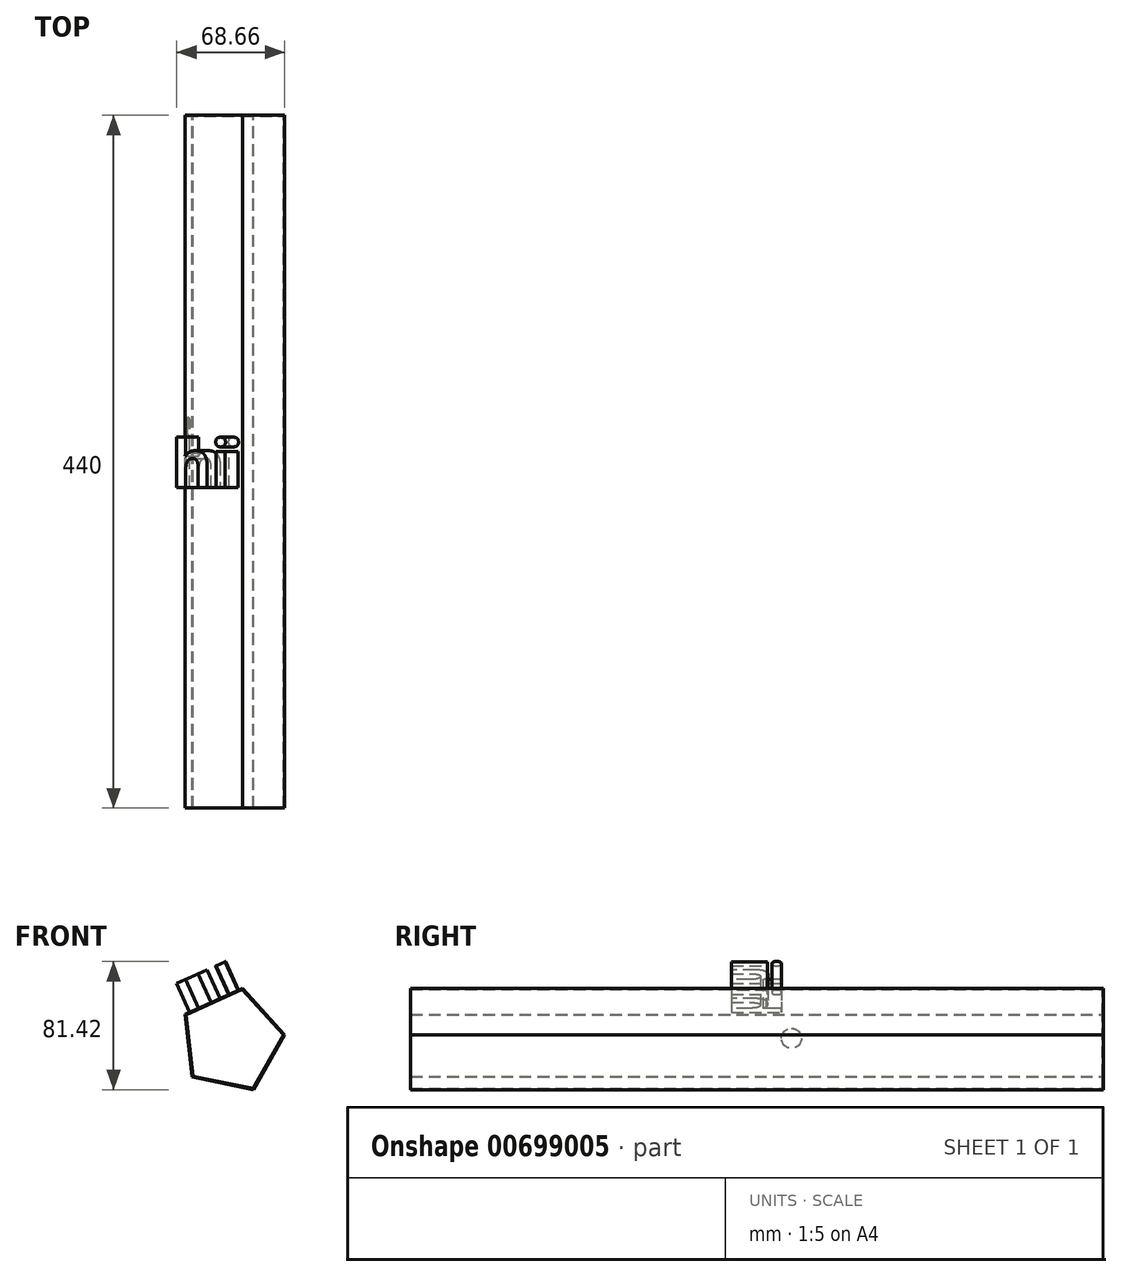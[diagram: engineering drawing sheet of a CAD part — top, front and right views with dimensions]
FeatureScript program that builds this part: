
annotation { "Feature Type Name" : "Feature", "Feature Type Description" : "" }
export const myFeature = defineFeature(function(context is Context, id is Id, definition is map)
    precondition{}
    {
        {
            var Q0;
            Q0=qCreatedBy(makeId("Front.planeOp"),FACE);
            var sketch = newSketch(context, id + "F0", { "sketchPlane" : qUnion([Q0])});
            skCircle(sketch, "E0.cCircle", {"center": v(19.03, -2.53) * mm, "radius": 27.53 * mm, "construction": true});
            skLineSegment(sketch, "E0.0", {"start": v(-10.54, 14.3) * mm, "end": v(25.9, 30.8) * mm});
            skLineSegment(sketch, "E0.1", {"start": v(25.9, 30.8) * mm, "end": v(52.85, 1.25) * mm});
            skLineSegment(sketch, "E0.2", {"start": v(52.85, 1.25) * mm, "end": v(33.07, -33.52) * mm});
            skLineSegment(sketch, "E0.3", {"start": v(33.07, -33.52) * mm, "end": v(-6.1, -25.46) * mm});
            skLineSegment(sketch, "E0.4", {"start": v(-6.1, -25.46) * mm, "end": v(-10.54, 14.3) * mm});
            skPoint(sketch, "E0.0.midPoint", {"position": v(7.68, 22.55) * mm});
            skSolve(sketch);
        }
        {
            var Q0;
            Q0=makeQuery(id+"F0.imprint","IMPRINT",FACE,{"disambiguationData":[TD([[makeQuery(id+"F0.imprint","IMPRINT",EDGE,{"derivedFrom":sQuery(id+"F0.wireOp",EDGE,"E0.0")}),-1.0]])]});
            extrude(context, id + "F1", {"entities" : qUnion([Q0]), "depth" : 440 * mm, "offsetDistance" : 25.4 * mm});
        }
        {
            var Q0;
            Q0=makeQuery(id+"F1.opExtrude","CAP_FACE",FACE,{"disambiguationData":[OSD([sQuery(id+"F0.wireOp",EDGE,"E0.0"),sQuery(id+"F0.wireOp",EDGE,"E0.1"),sQuery(id+"F0.wireOp",EDGE,"E0.2"),sQuery(id+"F0.wireOp",EDGE,"E0.3"),sQuery(id+"F0.wireOp",EDGE,"E0.4")])],"isStart":false});
            shell(context, id + "F2", {"entities" : qUnion([Q0]), "thickness" : .63 * mm});
        }
        {
            var Q0;
            Q0=makeQuery(id+"F1.opExtrude","SWEPT_FACE",FACE,{"disambiguationData":[OSD([sQuery(id+"F0.wireOp",EDGE,"E0.4")])]});
            var sketch = newSketch(context, id + "F3", { "sketchPlane" : qUnion([Q0])});
            skPoint(sketch, "E1", {"position": v(198.2, 0) * mm});
            skSolve(sketch);
        }
        {
            var Q0;
            Q0=sQuery(id+"F3.wireOp",VERTEX,"E1");
            var Q1;
            Q1=makeQuery(id+"F1.opExtrude","SWEPT_BODY",BODY,{"disambiguationData":[OSD([sQuery(id+"F0.wireOp",EDGE,"E0.0"),sQuery(id+"F0.wireOp",EDGE,"E0.1"),sQuery(id+"F0.wireOp",EDGE,"E0.2"),sQuery(id+"F0.wireOp",EDGE,"E0.3"),sQuery(id+"F0.wireOp",EDGE,"E0.4")])]});
            hole(context, id + "F4", {"style" : HoleStyle.SIMPLE, "endStyle" : HoleEndStyle.BLIND, "holeDiameter" : 12.7 * mm, "majorDiameter" : 6.35 * mm, "holeDepth" : 12.7 * mm, "isTappedThrough" : true, "tappedDepth" : 12.7 * mm, "tapClearance" : 3, "locations" : qUnion([Q0]), "scope" : qUnion([Q1])});
        }
        {
            var Q0;
            Q0=makeQuery(id+"F1.opExtrude","SWEPT_FACE",FACE,{"disambiguationData":[OSD([sQuery(id+"F0.wireOp",EDGE,"E0.0")])]});
            var sketch = newSketch(context, id + "F5", { "sketchPlane" : qUnion([Q0])});
            skText(sketch, "E2", { "text": "hi", "fontName": "OpenSans-Bold.ttf"});
            const initialGuessF5  = {"E2": [-0.0037, -0.2363, 1, 0, 0.03013]};
            skSetInitialGuess(sketch, initialGuessF5);
            skSolve(sketch);
        }
        {
            var Q0;
            Q0 = qSketchRegion(id + "F5", true);
            extrude(context, id + "F6", {"entities" : qUnion([Q0]), "operationType" : NewBodyOperationType.ADD, "depth" : 20 * mm, "offsetDistance" : 25 * mm});
        }
    });
